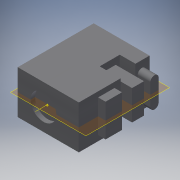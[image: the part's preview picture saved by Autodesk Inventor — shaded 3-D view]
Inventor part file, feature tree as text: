
AUTODESK INVENTOR PART (.ipt)
format: ipt  version: 2019.4 (Build 234330000, 330)  size: 148,992 bytes
history: native  units: mm
features: projected_geometry x4, extrude x3, sketch x3, other x2, plane x1
ambient origin geometry x8: Origin, YZ Plane, XZ Plane, XY Plane, X Axis, Y Axis, Z Axis, Center Point
bodies: Solid1 (feature_tree)
feature tree (13):
  extrude  "Extrusion1"  TaperAngle=0.0deg  [1 undecoded]
  extrude  "Extrusion2"  TaperAngle=90.0deg  [1 undecoded]
  extrude  "Extrusion3"  TaperAngle=90.0deg  [1 undecoded]
  plane  "Work Plane1"
  sketch  "Sketch1"  dims[d0=41.0mm d1=0.0mm]
  sketch  "Sketch2"  dims[d2=51.0mm d3=90.0deg]
  projected_geometry  "Projected Loop1"
  sketch  "Sketch3"  dims[d4=37.5mm d5=90.0deg d6=9.5mm d7=90.0deg d8=10.5mm d9=13.5mm d10=90.0deg d11=29.0mm d12=0.0mm d13=17.25mm d14=17.25mm d15=14.5mm d16=3.0mm d17=0.0mm d18=20.0mm d19=11.0mm d20=19.0mm d21=0.0mm]
  projected_geometry  "Projected Loop2"
  projected_geometry  "Projected Loop3"
  projected_geometry  "Projected Loop4"
  other  "Work Axis1"
  other  "Work Point1"
note: 3 required parameter values undecoded (feature->parameter linkage not recoverable at this tier; creation-order binding heuristic only, values carry confidence <= 0.55)
